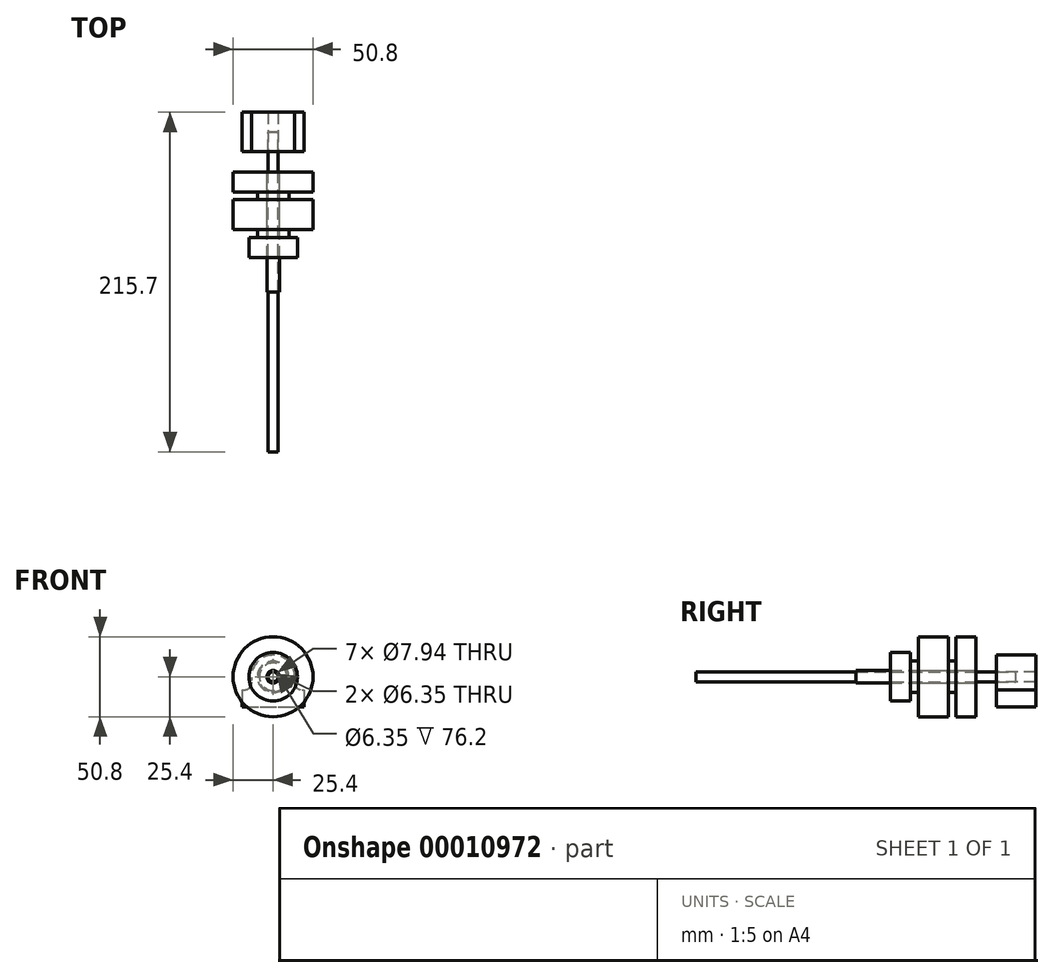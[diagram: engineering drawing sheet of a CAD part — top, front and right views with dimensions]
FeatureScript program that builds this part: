
annotation { "Feature Type Name" : "Feature", "Feature Type Description" : "" }
export const myFeature = defineFeature(function(context is Context, id is Id, definition is map)
    precondition{}
    {
        {
            var Q0;
            Q0=qCreatedBy(makeId("Front.planeOp"),FACE);
            var sketch = newSketch(context, id + "F0", { "sketchPlane" : qUnion([Q0])});
            skCircle(sketch, "E0", {"center": v(0, 0) * mm, "radius": 3.18 * mm});
            skSolve(sketch);
        }
        {
            var Q0;
            Q0=makeQuery(id+"F0.imprint","IMPRINT",FACE,{"disambiguationData":[TD([[makeQuery(id+"F0.imprint","IMPRINT",EDGE,{"derivedFrom":sQuery(id+"F0.wireOp",EDGE,"E0")}),1.0]])]});
            extrude(context, id + "F1", {"entities" : qUnion([Q0]), "depth" : 203.2 * mm});
        }
        {
            var Q0;
            Q0=qCreatedBy(makeId("Front.planeOp"),FACE);
            var sketch = newSketch(context, id + "F2", { "sketchPlane" : qUnion([Q0])});
            skCircle(sketch, "E1.0", {"center": v(0, 0) * mm, "radius": 3.18 * mm});
            skArc(sketch, "E2", {"start": v(13.53, -2.46) * mm, "mid": v(0, 13.75) * mm, "end": v(-13.53, -2.46) * mm});
            skLineSegment(sketch, "E3.rect.bottom", {"start": v(-19.73, -8.35) * mm, "end": v(-18.45, -8.35) * mm});
            skLineSegment(sketch, "E3.rect.top", {"start": v(-19.73, -19.15) * mm, "end": v(19.73, -19.15) * mm});
            skLineSegment(sketch, "E3.rect.left", {"start": v(-19.73, -8.35) * mm, "end": v(-19.73, -19.15) * mm});
            skLineSegment(sketch, "E3.rect.right", {"start": v(19.73, -8.35) * mm, "end": v(19.73, -19.15) * mm});
            skPoint(sketch, "E3.rect.middle", {"position": v(0, -13.75) * mm});
            skLineSegment(sketch, "E4.trimOffspring", {"start": v(18.45, -8.35) * mm, "end": v(19.73, -8.35) * mm});
            skPoint(sketch, "E5.visualSharp", {"position": v(-10.92, -8.35) * mm});
            skArc(sketch, "E5.filletArc", {"start": v(-18.45, -8.35) * mm, "mid": v(-14.6, -6.56) * mm, "end": v(-13.53, -2.46) * mm});
            skPoint(sketch, "E6.visualSharp", {"position": v(10.92, -8.35) * mm});
            skArc(sketch, "E6.filletArc", {"start": v(13.53, -2.46) * mm, "mid": v(14.6, -6.56) * mm, "end": v(18.45, -8.35) * mm});
            skSolve(sketch);
        }
        {
            var Q0;
            Q0=makeQuery(id+"F2.imprint","IMPRINT",FACE,{"disambiguationData":[TD([[makeQuery(id+"F2.imprint","IMPRINT",EDGE,{"derivedFrom":sQuery(id+"F2.wireOp",EDGE,"E1.0")}),-1.0]])]});
            extrude(context, id + "F3", {"entities" : qUnion([Q0]), "endBound" : BoundingType.SYMMETRIC, "oppositeDirection" : true, "depth" : 25 * mm});
        }
        {
            var Q0;
            Q0=qCreatedBy(makeId("Front.planeOp"),FACE);
            cPlane(context, id + "F4", {"entities" : qUnion([Q0]), "cplaneType" : CPlaneType.OFFSET, "offset" : 25.4 * mm, "width" : 150 * mm, "height" : 150 * mm});
        }
        {
            var Q0;
            Q0=qCreatedBy(id+"F4.planeOp",FACE);
            var sketch = newSketch(context, id + "F5", { "sketchPlane" : qUnion([Q0])});
            skCircle(sketch, "E7", {"center": v(0, 0) * mm, "radius": 8.73 * mm});
            skCircle(sketch, "E8.0", {"center": v(0, 0) * mm, "radius": 3.18 * mm});
            skSolve(sketch);
        }
        {
            var Q0;
            Q0=makeQuery(id+"F5.imprint","IMPRINT",FACE,{"disambiguationData":[TD([[makeQuery(id+"F5.imprint","IMPRINT",EDGE,{"derivedFrom":sQuery(id+"F5.wireOp",EDGE,"E7")}),1.0]])]});
            extrude(context, id + "F6", {"entities" : qUnion([Q0]), "depth" : 5 / 406.4 * mm});
        }
        {
            var Q0;
            Q0=makeQuery(id+"F6.opExtrude","CAP_FACE",FACE,{"disambiguationData":[OSD([sQuery(id+"F5.wireOp",EDGE,"E7"),sQuery(id+"F5.wireOp",EDGE,"E8.0")])],"isStart":false});
            var sketch = newSketch(context, id + "F7", { "sketchPlane" : qUnion([Q0])});
            skSolve(sketch);
        }
        {
            var Q0;
            Q0=makeQuery(id+"F7.imprint","IMPRINT",FACE,{"disambiguationData":[TD([[makeQuery(id+"F7.imprint","IMPRINT",EDGE,{"derivedFrom":makeQuery(id+"F6.opExtrude","CAP_EDGE",EDGE,{"disambiguationData":[OSD([sQuery(id+"F5.wireOp",EDGE,"E7")])],"isStart":false})}),1.0]])]});
            var sketch = newSketch(context, id + "F8", { "sketchPlane" : qUnion([Q0])});
            skCircle(sketch, "E9.0", {"center": v(0, 0) * mm, "radius": 3.18 * mm});
            skCircle(sketch, "E10", {"center": v(0, 0) * mm, "radius": 3.97 * mm});
            skSolve(sketch);
        }
        {
            var Q0;
            Q0 = qSketchRegion(id + "F8", true);
            extrude(context, id + "F9", {"entities" : qUnion([Q0]), "depth" : 76.2 * mm});
        }
        {
            var Q0;
            Q0=makeQuery(id+"F6.opExtrude","CAP_FACE",FACE,{"disambiguationData":[OSD([sQuery(id+"F5.wireOp",EDGE,"E7"),sQuery(id+"F5.wireOp",EDGE,"E8.0")])],"isStart":false});
            var sketch = newSketch(context, id + "F10", { "sketchPlane" : qUnion([Q0])});
            skCircle(sketch, "E11.0", {"center": v(0, 0) * mm, "radius": 3.97 * mm});
            skCircle(sketch, "E12", {"center": v(0, 0) * mm, "radius": 9.5 * mm});
            skSolve(sketch);
        }
        {
            var Q0;
            Q0=makeQuery(id+"F10.imprint","IMPRINT",FACE,{"disambiguationData":[TD([[makeQuery(id+"F10.imprint","IMPRINT",EDGE,{"derivedFrom":sQuery(id+"F10.wireOp",EDGE,"E12")}),1.0]])]});
            var Q1;
            Q1=makeQuery(id+"F10.imprint","IMPRINT",FACE,{"disambiguationData":[TD([[makeQuery(id+"F10.imprint","IMPRINT",EDGE,{"derivedFrom":sQuery(id+"F10.wireOp",EDGE,"E11.0")}),-1.0]])]});
            extrude(context, id + "F11", {"entities" : qUnion([Q0, Q1]), "depth" : 5 / 406.4 * mm});
        }
        {
            var Q0;
            Q0=makeQuery(id+"F11.opExtrude","CAP_FACE",FACE,{"disambiguationData":[OSD([sQuery(id+"F10.wireOp",EDGE,"E11.0"),sQuery(id+"F10.wireOp",EDGE,"E12")])],"isStart":false});
            var sketch = newSketch(context, id + "F12", { "sketchPlane" : qUnion([Q0])});
            skCircle(sketch, "E13", {"center": v(0, 0) * mm, "radius": 25.4 * mm});
            skSolve(sketch);
        }
        {
            var Q0;
            Q0=makeQuery(id+"F12.imprint","IMPRINT",FACE,{"disambiguationData":[TD([[makeQuery(id+"F12.imprint","IMPRINT",EDGE,{"derivedFrom":sQuery(id+"F12.wireOp",EDGE,"E13")}),1.0]])]});
            var Q1;
            Q1=makeQuery(id+"F12.imprint","IMPRINT",FACE,{"disambiguationData":[TD([[makeQuery(id+"F12.imprint","IMPRINT",EDGE,{"derivedFrom":makeQuery(id+"F11.opExtrude","CAP_EDGE",EDGE,{"disambiguationData":[OSD([sQuery(id+"F10.wireOp",EDGE,"E11.0")])],"isStart":false})}),-1.0]])]});
            extrude(context, id + "F13", {"entities" : qUnion([Q0, Q1]), "depth" : 12.7 * mm});
        }
        {
            var Q0;
            Q0=makeQuery(id+"F13.opExtrude","CAP_FACE",FACE,{"disambiguationData":[OSD([sQuery(id+"F10.wireOp",EDGE,"E11.0"),sQuery(id+"F12.wireOp",EDGE,"E13")])],"isStart":false});
            var sketch = newSketch(context, id + "F14", { "sketchPlane" : qUnion([Q0])});
            skCircle(sketch, "E14.0", {"center": v(0, 0) * mm, "radius": 3.97 * mm});
            skCircle(sketch, "E15", {"center": v(0, 0) * mm, "radius": 10 * mm});
            skSolve(sketch);
        }
        {
            var Q0;
            Q0=makeQuery(id+"F14.imprint","IMPRINT",FACE,{"disambiguationData":[TD([[makeQuery(id+"F14.imprint","IMPRINT",EDGE,{"derivedFrom":sQuery(id+"F14.wireOp",EDGE,"E14.0")}),-1.0]])]});
            extrude(context, id + "F15", {"entities" : qUnion([Q0]), "depth" : 5 * mm});
        }
        {
            var Q0;
            Q0=makeQuery(id+"F15.opExtrude","CAP_FACE",FACE,{"disambiguationData":[OSD([sQuery(id+"F14.wireOp",EDGE,"E14.0"),sQuery(id+"F14.wireOp",EDGE,"E15")])],"isStart":false});
            var sketch = newSketch(context, id + "F16", { "sketchPlane" : qUnion([Q0])});
            skCircle(sketch, "E16.0", {"center": v(0, 0) * mm, "radius": 3.97 * mm});
            skCircle(sketch, "E17", {"center": v(0, 0) * mm, "radius": 25.4 * mm});
            skSolve(sketch);
        }
        {
            var Q0;
            Q0=makeQuery(id+"F16.imprint","IMPRINT",FACE,{"disambiguationData":[TD([[makeQuery(id+"F16.imprint","IMPRINT",EDGE,{"derivedFrom":sQuery(id+"F16.wireOp",EDGE,"E17")}),1.0]])]});
            var Q1;
            Q1=makeQuery(id+"F16.imprint","IMPRINT",FACE,{"disambiguationData":[TD([[makeQuery(id+"F16.imprint","IMPRINT",EDGE,{"derivedFrom":sQuery(id+"F16.wireOp",EDGE,"E16.0")}),-1.0]])]});
            extrude(context, id + "F17", {"entities" : qUnion([Q0, Q1]), "depth" : 19.05 * mm});
        }
        {
            var Q0;
            Q0=makeQuery(id+"F17.opExtrude","CAP_FACE",FACE,{"disambiguationData":[OSD([sQuery(id+"F16.wireOp",EDGE,"E16.0"),sQuery(id+"F16.wireOp",EDGE,"E17")])],"isStart":false});
            var sketch = newSketch(context, id + "F18", { "sketchPlane" : qUnion([Q0])});
            skCircle(sketch, "E18.0", {"center": v(0, 0) * mm, "radius": 10 * mm});
            skCircle(sketch, "E18.1", {"center": v(0, 0) * mm, "radius": 3.97 * mm});
            skSolve(sketch);
        }
        {
            var Q0;
            Q0=makeQuery(id+"F18.imprint","IMPRINT",FACE,{"disambiguationData":[TD([[makeQuery(id+"F18.imprint","IMPRINT",EDGE,{"derivedFrom":sQuery(id+"F18.wireOp",EDGE,"E18.0")}),1.0]])]});
            extrude(context, id + "F19", {"entities" : qUnion([Q0]), "depth" : 5 * mm});
        }
        {
            var Q0;
            Q0=makeQuery(id+"F19.opExtrude","CAP_FACE",FACE,{"disambiguationData":[OSD([sQuery(id+"F18.wireOp",EDGE,"E18.0"),sQuery(id+"F18.wireOp",EDGE,"E18.1")])],"isStart":false});
            var sketch = newSketch(context, id + "F20", { "sketchPlane" : qUnion([Q0])});
            skCircle(sketch, "E19.0", {"center": v(0, 0) * mm, "radius": 9.5 * mm});
            skCircle(sketch, "E20.0", {"center": v(0, 0) * mm, "radius": 3.97 * mm});
            skSolve(sketch);
        }
        {
            var Q0;
            Q0=makeQuery(id+"F20.imprint","IMPRINT",FACE,{"disambiguationData":[TD([[makeQuery(id+"F20.imprint","IMPRINT",EDGE,{"derivedFrom":sQuery(id+"F20.wireOp",EDGE,"E19.0")}),1.0]])]});
            extrude(context, id + "F21", {"entities" : qUnion([Q0]), "depth" : 5 / 406.4 * mm});
        }
        {
            var Q0;
            Q0=makeQuery(id+"F21.opExtrude","CAP_FACE",FACE,{"disambiguationData":[OSD([sQuery(id+"F20.wireOp",EDGE,"E19.0"),sQuery(id+"F20.wireOp",EDGE,"E20.0")])],"isStart":false});
            var sketch = newSketch(context, id + "F22", { "sketchPlane" : qUnion([Q0])});
            skCircle(sketch, "E21.0", {"center": v(0, 0) * mm, "radius": 3.97 * mm});
            skCircle(sketch, "E22", {"center": v(0, 0) * mm, "radius": 15.4 * mm});
            skSolve(sketch);
        }
        {
            var Q0;
            Q0=makeQuery(id+"F22.imprint","IMPRINT",FACE,{"disambiguationData":[TD([[makeQuery(id+"F22.imprint","IMPRINT",EDGE,{"derivedFrom":sQuery(id+"F22.wireOp",EDGE,"E22")}),1.0]])]});
            var Q1;
            Q1=makeQuery(id+"F22.imprint","IMPRINT",FACE,{"disambiguationData":[TD([[makeQuery(id+"F22.imprint","IMPRINT",EDGE,{"derivedFrom":sQuery(id+"F22.wireOp",EDGE,"E21.0")}),-1.0]])]});
            extrude(context, id + "F23", {"entities" : qUnion([Q0, Q1]), "depth" : 12.7 * mm});
        }
    });
